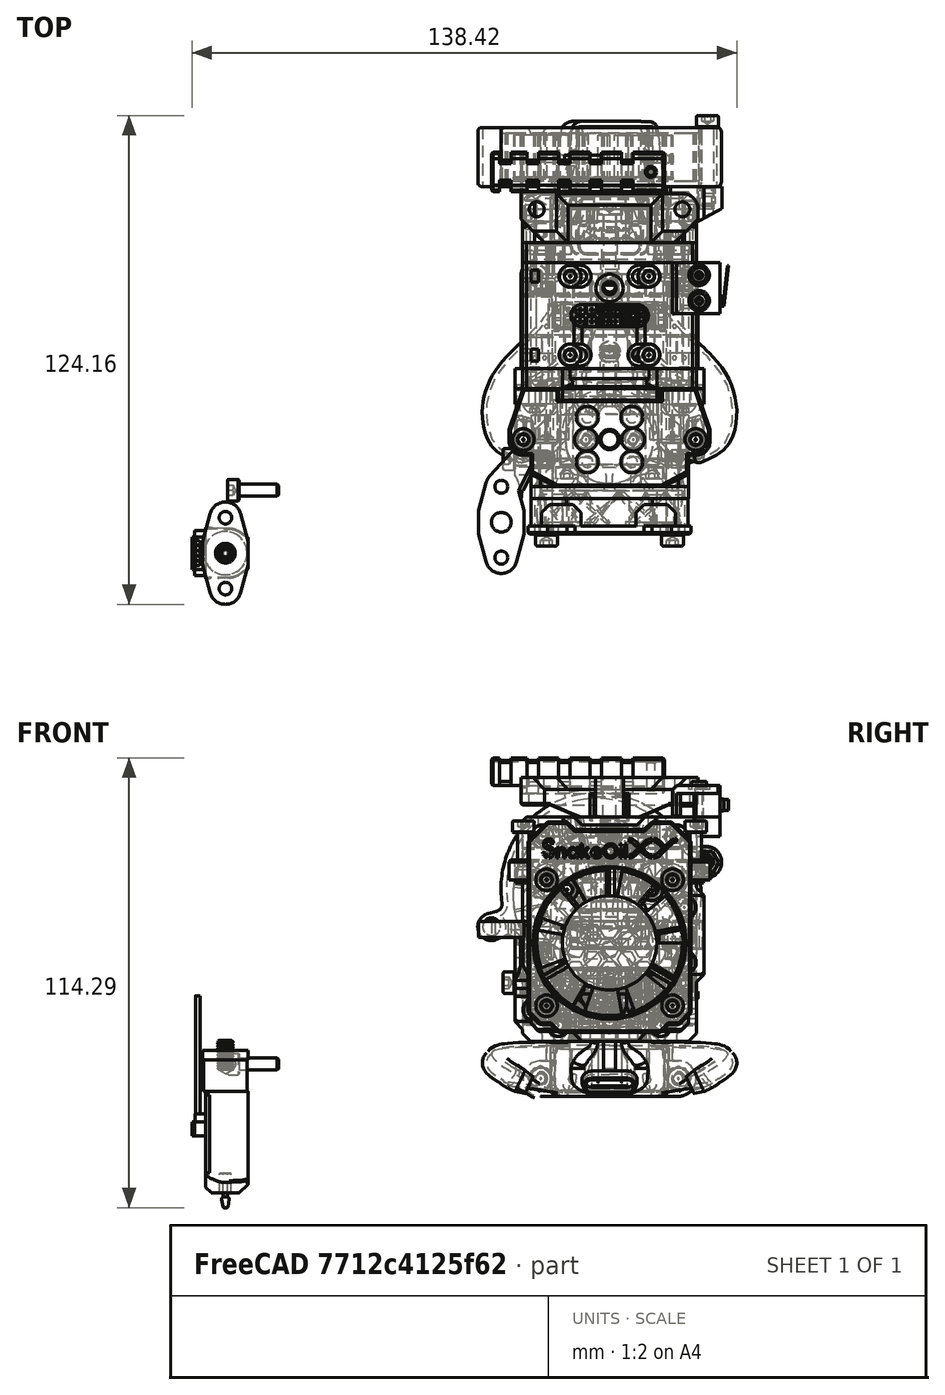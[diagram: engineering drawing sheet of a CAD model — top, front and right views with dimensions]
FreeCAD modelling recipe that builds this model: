
FCSTD DOCUMENT  (FreeCAD 0.19R)
Label: toolhead-sherpa-pcb-1515-assembly
License: Other
LicenseURL: GPL3
objects: Part::FeaturePython×59, Part::Feature×32, App::Part×13, PartDesign::CoordinateSystem×1
note: 92 computed .brp shape members not serialized (recipe doc carries the construction recipe); baked Part::Feature solids carry a one-line shape summary decoded from their .brp

FEATURE [Part::FeaturePython] Screw1373  label="M3x20-Screw024"  # Fasteners workbench fastener (typed FeaturePython)
  Placement = pos=(16,-55.5,30) rot=(1,0,0;1.5708rad)
  baseObject = -> Part__Feature112001131 [Edge124]
  diameter = 4
  invert = false
  leftHanded = false
  length = 10
  lengthCustom = 20
  matchOuter = true
  offset = 2
  thread = false
  type = 33
FEATURE [Part::FeaturePython] Screw1374  label="M3x25-Screw004"  # Fasteners workbench fastener (typed FeaturePython)
  Placement = pos=(-16,-55.5,-2) rot=(1,0,0;1.5708rad)
  baseObject = -> Part__Feature112001131 [Edge127]
  diameter = 4
  invert = false
  leftHanded = false
  length = 10
  lengthCustom = 25
  matchOuter = true
  offset = 2
  thread = false
  type = 33
FEATURE [Part::FeaturePython] Screw1375  label="M3x25-Screw029"  # Fasteners workbench fastener (typed FeaturePython)
  Placement = pos=(16,-55.5,-2) rot=(1,0,0;1.5708rad)
  baseObject = -> Part__Feature112001131 [Edge121]
  diameter = 4
  invert = false
  leftHanded = false
  length = 10
  lengthCustom = 25
  matchOuter = true
  offset = 2
  thread = false
  type = 33
FEATURE [Part::FeaturePython] Screw1376  label="M2.5x12-Screw"  # Fasteners workbench fastener (typed FeaturePython)
  Placement = pos=(-6,-31.5,29.2) rot=(0,0,1;0rad)
  diameter = 3
  invert = false
  leftHanded = false
  length = 10
  lengthCustom = 12
  matchOuter = true
  offset = 10
  thread = false
  type = 33
FEATURE [Part::FeaturePython] Screw1377  label="M2.5x12-Screw001"  # Fasteners workbench fastener (typed FeaturePython)
  Placement = pos=(6,-31.5,29.2) rot=(0,0,1;0rad)
  diameter = 3
  invert = false
  leftHanded = false
  length = 10
  lengthCustom = 12
  matchOuter = true
  offset = 10
  thread = false
  type = 33
FEATURE [Part::FeaturePython] Screw1372  label="M3x20-Screw023"  # Fasteners workbench fastener (typed FeaturePython)
  Placement = pos=(-16,-55.5,30) rot=(1,0,0;1.5708rad)
  baseObject = -> Part__Feature112001131 [Edge130]
  diameter = 4
  invert = false
  leftHanded = false
  length = 10
  lengthCustom = 20
  matchOuter = true
  offset = 2
  thread = false
  type = 33
FEATURE [Part::Feature] Part__Feature112001131  label="4010-fan"
  Placement = pos=(-2.4e-14,-43.5,14) rot=(0,0,1;0rad)
  shape: bbox 40 x 10 x 40 mm, 104 faces (baked)
FEATURE [Part::Feature] Part__Feature112001139  label="BL-touch v3.x002"
  Placement = pos=(-97.5942,-60.3565,-13.2887) rot=(0,0,1;1.5708rad)
  shape: bbox 16.53 x 26.01 x 53.81 mm, 111 faces (baked)
FEATURE [Part::FeaturePython] Nut057  label="M3-Nut026"  # Fasteners workbench fastener (typed FeaturePython)
  Placement = pos=(-17.05,15.5,41) rot=(-1,0,0;1.5708rad)
  diameter = 4
  invert = false
  leftHanded = false
  matchOuter = true
  offset = 0
  thread = false
  type = 7
FEATURE [Part::FeaturePython] Nut004  label="M3-Nut009"  # Fasteners workbench fastener (typed FeaturePython)
  Placement = pos=(13,15.5,-7) rot=(-1,0,0;1.5708rad)
  diameter = 4
  invert = false
  leftHanded = false
  matchOuter = true
  offset = 0
  thread = false
  type = 7
FEATURE [Part::FeaturePython] Nut005  label="M3-Nut030"  # Fasteners workbench fastener (typed FeaturePython)
  Placement = pos=(-13,15.5,-7) rot=(-1,0,0;1.5708rad)
  diameter = 4
  invert = false
  leftHanded = false
  matchOuter = true
  offset = 0
  thread = false
  type = 7
FEATURE [Part::FeaturePython] Screw1359  label="M3x35-Screw004"  # Fasteners workbench fastener (typed FeaturePython)
  Placement = pos=(-13.0042,-16,-6.99647) rot=(1,0,0;1.5708rad)
  diameter = 4
  invert = true
  leftHanded = false
  length = 10
  lengthCustom = 35
  matchOuter = true
  offset = 0
  thread = false
  type = 33
FEATURE [Part::FeaturePython] Screw1360  label="M3x35-Screw003"  # Fasteners workbench fastener (typed FeaturePython)
  Placement = pos=(12.9958,-16,-6.99647) rot=(1,0,0;1.5708rad)
  diameter = 4
  invert = true
  leftHanded = false
  length = 10
  lengthCustom = 35
  matchOuter = true
  offset = 0
  thread = false
  type = 33
FEATURE [Part::FeaturePython] Screw020  label="M3x10-Screw"  # Fasteners workbench fastener (typed FeaturePython)
  Placement = pos=(-10.0042,-9.99647,39.1513) rot=(0,0,1;0rad)
  diameter = 4
  invert = false
  leftHanded = false
  length = 10
  lengthCustom = 10
  matchOuter = true
  offset = 0
  thread = false
  type = 33
FEATURE [Part::FeaturePython] Screw022  label="M3x12-Screw"  # Fasteners workbench fastener (typed FeaturePython)
  Placement = pos=(-21.9,-31.5,42) rot=(0,0,1;0rad)
  diameter = 4
  invert = false
  leftHanded = false
  length = 10
  lengthCustom = 12
  matchOuter = true
  offset = 7
  thread = false
  type = 33
FEATURE [Part::FeaturePython] Screw023  label="M3x12-Screw066"  # Fasteners workbench fastener (typed FeaturePython)
  Placement = pos=(21.9,-31.5,42) rot=(0,0,1;0rad)
  diameter = 4
  invert = false
  leftHanded = false
  length = 10
  lengthCustom = 12
  matchOuter = true
  offset = 7
  thread = false
  type = 33
FEATURE [Part::FeaturePython] Screw026  label="M3x10-Screw199"  # Fasteners workbench fastener (typed FeaturePython)
  Placement = pos=(3e-15,-20.15,-6) rot=(1,0,0;1.5708rad)
  baseObject = -> Part__Feature112001133 [Edge213]
  diameter = 4
  invert = true
  leftHanded = false
  length = 3
  lengthCustom = 10
  matchOuter = true
  offset = 0
  thread = false
  type = 33
FEATURE [Part::FeaturePython] Screw027  label="M3x25-Screw"  # Fasteners workbench fastener (typed FeaturePython)
  Placement = pos=(-10.8,-38.5,27.5) rot=(1,0,0;1.5708rad)
  diameter = 4
  invert = false
  leftHanded = false
  length = 10
  lengthCustom = 25
  matchOuter = true
  offset = 0
  thread = false
  type = 33
FEATURE [Part::FeaturePython] Screw1369  label="M3x25-Screw030"  # Fasteners workbench fastener (typed FeaturePython)
  Placement = pos=(10.8,-38.5,27.5) rot=(1,0,0;1.5708rad)
  diameter = 4
  invert = false
  leftHanded = false
  length = 10
  lengthCustom = 25
  matchOuter = true
  offset = 0
  thread = false
  type = 33
FEATURE [Part::FeaturePython] Nut058  label="M3-Nut027"  # Fasteners workbench fastener (typed FeaturePython)
  Placement = pos=(17.05,15.5,41) rot=(-1,0,0;1.5708rad)
  diameter = 4
  invert = false
  leftHanded = false
  matchOuter = true
  offset = 0
  thread = false
  type = 7
FEATURE [Part::FeaturePython] Screw1355  label="M3x40-Screw001"  # Fasteners workbench fastener (typed FeaturePython)
  Placement = pos=(-18.5,25.5,3.5) rot=(0,-1,0;1.5708rad)
  diameter = 4
  invert = false
  leftHanded = false
  length = 10
  lengthCustom = 40
  matchOuter = true
  offset = 0
  thread = false
  type = 33
FEATURE [Part::FeaturePython] Screw1356  label="M3x40-Screw"  # Fasteners workbench fastener (typed FeaturePython)
  Placement = pos=(18.5,25.5,16.5) rot=(0,1,0;1.5708rad)
  diameter = 4
  invert = false
  leftHanded = false
  length = 10
  lengthCustom = 40
  matchOuter = true
  offset = 0
  thread = false
  type = 33
FEATURE [Part::Feature] Fusion006002011004053036004001028003005014018035002010  label="mosquito-hotend"
  Placement = pos=(0,-31.5,-28) rot=(0,0,1;0rad)
  shape: bbox 27.01 x 18.86 x 47.01 mm, 355 faces, 0 solids (baked)
FEATURE [Part::Feature] Part__Feature112001133  label="mosquito_support"
  Placement = pos=(-2.78e-14,-21.6,27.5) rot=(0,0,1;0rad)
  shape: bbox 40 x 20.25 x 12 mm, 97 faces (baked)
FEATURE [Part::Feature] Part__Feature112001136  label="5015 fan"
  Placement = pos=(-4.23967,32.8,25.9455) rot=(0.15487,0.698575,0.698575;3.44889rad)
  shape: bbox 61.97 x 15 x 62.93 mm, 220 faces (baked)
FEATURE [Part::FeaturePython] Screw1368  label="M3x20-Screw"  # Fasteners workbench fastener (typed FeaturePython)
  Placement = pos=(24.8765,47.8,34.436) rot=(-1,0,0;1.5708rad)
  baseObject = -> Part__Feature112001136 [Edge8]
  diameter = 4
  invert = false
  leftHanded = false
  length = 7
  lengthCustom = 20
  matchOuter = true
  offset = 0
  thread = false
  type = 33
FEATURE [Part::FeaturePython] Screw017  label="M3x10-Screw188"  # Fasteners workbench fastener (typed FeaturePython)
  Placement = pos=(9.99577,10.0035,39.1513) rot=(0,0,1;0rad)
  diameter = 4
  invert = true
  leftHanded = false
  length = 10
  lengthCustom = 10
  matchOuter = true
  offset = 0
  thread = false
  type = 33
FEATURE [Part::FeaturePython] Screw018  label="M3x10-Screw186"  # Fasteners workbench fastener (typed FeaturePython)
  Placement = pos=(9.99577,-9.99647,39.1513) rot=(0,0,1;0rad)
  diameter = 4
  invert = true
  leftHanded = false
  length = 10
  lengthCustom = 10
  matchOuter = true
  offset = 0
  thread = false
  type = 33
FEATURE [Part::FeaturePython] Screw019  label="M3x10-Screw187"  # Fasteners workbench fastener (typed FeaturePython)
  Placement = pos=(-10.0042,10.0035,39.1513) rot=(0,0,1;0rad)
  diameter = 4
  invert = false
  leftHanded = false
  length = 10
  lengthCustom = 10
  matchOuter = true
  offset = 0
  thread = false
  type = 33
FEATURE [Part::FeaturePython] Screw1380  label="M3x35-Screw005"  # Fasteners workbench fastener (typed FeaturePython)
  Placement = pos=(-17.0542,-16.5,41.0035) rot=(1,0,0;1.5708rad)
  diameter = 1
  invert = true
  leftHanded = false
  length = 9
  lengthCustom = 35
  matchOuter = true
  offset = 0
  thread = false
  type = 39
FEATURE [Part::FeaturePython] Screw1381  label="M3x35-Screw"  # Fasteners workbench fastener (typed FeaturePython)
  Placement = pos=(17.0458,-16.5,41.0035) rot=(1,0,0;1.5708rad)
  diameter = 1
  invert = true
  leftHanded = false
  length = 9
  lengthCustom = 35
  matchOuter = true
  offset = 0
  thread = false
  type = 39
FEATURE [Part::Feature] Part__Feature112001143  label="dragon_support"
  Placement = pos=(-1.3e-14,-65.5,-44.5) rot=(1,0,0;3.14159rad)
  shape: bbox 40 x 20.25 x 9.266 mm, 50 faces (baked)
FEATURE [Part::Feature] Chamfer005021077002006007019003014001  label="face-plate"
  Placement = pos=(0,-56.5,-6) rot=(0,0,1;0rad)
  shape: bbox 41.5 x 7.5 x 53.5 mm, 789 faces (baked)
FEATURE [Part::Feature] Chamfer005021077002006007019003032007001  label="mosquito-mount-mod"
  Placement = pos=(0,-31.5,33) rot=(0,0,1;0rad)
  shape: bbox 51.01 x 27.77 x 40.81 mm, 154 faces (baked)
FEATURE [Part::Feature] Chamfer005021077002006007019003029001  label="dragon-mount-mod"
  Placement = pos=(0,-31.5,33) rot=(0,0,1;0rad)
  shape: bbox 51.01 x 26.2 x 43.01 mm, 143 faces (baked)
FEATURE [Part::FeaturePython] Screw1371  label="M3x10-Screw189"  # Fasteners workbench fastener (typed FeaturePython)
  Placement = pos=(-94.0942,-44.3565,-16.7887) rot=(0,-1,0;1.5708rad)
  diameter = 4
  invert = false
  leftHanded = false
  length = 10
  lengthCustom = 10
  matchOuter = true
  offset = 0
  thread = false
  type = 33
FEATURE [App::Part] BL_Touch__1_001  label="BL-Touch <1>001"
  Group = -> [Part__Feature112001139,Screw1371]
  Origin = -> Origin206
  Placement = pos=(70,8,28.5) rot=(0,0,1;0rad)
FEATURE [Part::Feature] Chamfer008009001  label="extruder-belt-tesioner"
  Placement = pos=(6,15,7.5) rot=(0,1,0;3.14159rad)
  shape: bbox 20 x 14.4 x 10 mm, 116 faces (baked)
FEATURE [Part::Feature] Chamfer005021077002006007019003032007003  label="extruder-belt-tesioner001"
  Placement = pos=(-6,15,12.5) rot=(0,0,1;0rad)
  shape: bbox 20 x 14.4 x 10 mm, 116 faces (baked)
FEATURE [Part::Feature] Fusion006002011004053036004001028003005014029  label="endstop-switch"
  Placement = pos=(28,7,46) rot=(0,0,1;1.5708rad)
  shape: bbox 12.18 x 13 x 6 mm, 43 faces (baked)
FEATURE [Part::Feature] Body001001001  label="endstop-cap"
  Placement = pos=(16,7,54) rot=(1,0,0;3.14159rad)
  shape: bbox 12 x 13 x 7.75 mm, 19 faces (baked)
FEATURE [Part::FeaturePython] Screw1382  label="M2x10-Screw001"  # Fasteners workbench fastener (typed FeaturePython)
  Placement = pos=(22.75,3.75,53) rot=(0,0,1;0rad)
  baseObject = -> Body001001001 [Edge27]
  diameter = 2
  invert = false
  leftHanded = false
  length = 5
  lengthCustom = 10
  matchOuter = true
  offset = 0
  thread = false
  type = 33
FEATURE [Part::FeaturePython] Screw1383  label="M2x10-Screw"  # Fasteners workbench fastener (typed FeaturePython)
  Placement = pos=(22.75,10.25,53) rot=(0,0,1;0rad)
  baseObject = -> Body001001001 [Edge25]
  diameter = 2
  invert = false
  leftHanded = false
  length = 5
  lengthCustom = 10
  matchOuter = true
  offset = 0
  thread = false
  type = 33
FEATURE [PartDesign::CoordinateSystem] LCS_toolhead_1515  label="LCS_toolhead-1515"
  AttacherType = Attacher::AttachEngine3D
FEATURE [Part::FeaturePython] HeatSet001  label="M3x4-HeatSet001"  # Fasteners workbench fastener (typed FeaturePython)
  Placement = pos=(-20,-36.5,11.7) rot=(0,-1,0;1.5708rad)
  baseObject = -> Chamfer005021077002006007019003029001 [Edge194]
  diameter = 2
  invert = false
  leftHanded = false
  matchOuter = false
  offset = 0
  thread = false
  type = 25
FEATURE [Part::FeaturePython] HeatSet002  label="M3x4-HeatSet003"  # Fasteners workbench fastener (typed FeaturePython)
  Placement = pos=(20,-36.5,11.7) rot=(0,1,0;1.5708rad)
  baseObject = -> Chamfer005021077002006007019003029001 [Edge128]
  diameter = 2
  invert = true
  leftHanded = false
  matchOuter = false
  offset = 0
  thread = false
  type = 25
FEATURE [Part::FeaturePython] HeatSet003  label="M3x4-HeatSet"  # Fasteners workbench fastener (typed FeaturePython)
  Placement = pos=(20,-36.5,3.7) rot=(0,1,0;1.5708rad)
  baseObject = -> Chamfer005021077002006007019003029001 [Edge127]
  diameter = 2
  invert = true
  leftHanded = false
  matchOuter = false
  offset = 0
  thread = false
  type = 25
FEATURE [Part::FeaturePython] HeatSet004  label="M3x4-HeatSet009"  # Fasteners workbench fastener (typed FeaturePython)
  Placement = pos=(1e-14,7.5,46) rot=(0,0,1;0rad)
  diameter = 2
  invert = true
  leftHanded = false
  matchOuter = false
  offset = 0
  thread = false
  type = 25
FEATURE [Part::FeaturePython] HeatSet014  label="M3x4-HeatSet010"  # Fasteners workbench fastener (typed FeaturePython)
  Placement = pos=(10.8,-13.5,27.705) rot=(-1,0,0;1.5708rad)
  diameter = 2
  invert = true
  leftHanded = false
  matchOuter = false
  offset = 0
  thread = false
  type = 25
FEATURE [Part::FeaturePython] HeatSet015  label="M3x4-HeatSet012"  # Fasteners workbench fastener (typed FeaturePython)
  Placement = pos=(-10.8,-13.5,27.71) rot=(-1,0,0;1.5708rad)
  diameter = 2
  invert = true
  leftHanded = false
  matchOuter = false
  offset = 0
  thread = false
  type = 25
FEATURE [Part::FeaturePython] HeatSet016  label="M3x4-HeatSet004"  # Fasteners workbench fastener (typed FeaturePython)
  Placement = pos=(10,25.5,3.5) rot=(0,1,0;1.5708rad)
  baseObject = -> Chamfer008009001 [Edge5]
  diameter = 2
  invert = false
  leftHanded = false
  matchOuter = false
  offset = 0
  thread = false
  type = 25
FEATURE [Part::FeaturePython] HeatSet017  label="M3x4-HeatSet013"  # Fasteners workbench fastener (typed FeaturePython)
  Placement = pos=(-10,25.5,16.5) rot=(0,-1,0;1.5708rad)
  baseObject = -> Chamfer005021077002006007019003032007003 [Edge5]
  diameter = 2
  invert = false
  leftHanded = false
  matchOuter = false
  offset = 0
  thread = false
  type = 25
FEATURE [Part::FeaturePython] HeatSet018  label="M3x4-HeatSet018"  # Fasteners workbench fastener (typed FeaturePython)
  Placement = pos=(21.9,-31.5,35) rot=(0,0,1;0rad)
  baseObject = -> Chamfer005021077002006007019003029001 [Edge25]
  diameter = 2
  invert = false
  leftHanded = false
  matchOuter = false
  offset = 0
  thread = false
  type = 25
FEATURE [Part::FeaturePython] HeatSet019  label="M3x4-HeatSet017"  # Fasteners workbench fastener (typed FeaturePython)
  Placement = pos=(-21.9,-31.5,35) rot=(0,0,1;0rad)
  baseObject = -> Chamfer005021077002006007019003029001 [Edge1]
  diameter = 2
  invert = false
  leftHanded = false
  matchOuter = false
  offset = 0
  thread = false
  type = 25
FEATURE [Part::Feature] Part__Feature003  label="duct-tri-horn"
  Placement = pos=(0,10.5978,-18) rot=(1,0,0;1.5708rad)
  shape: bbox 65.34 x 50.74 x 15.61 mm, 106 faces (baked)
FEATURE [Part::FeaturePython] Nut059  label="M3-Nut032"  # Fasteners workbench fastener (typed FeaturePython)
  Placement = pos=(-17.5,8.59783,-20.5) rot=(1,0,0;1.5708rad)
  baseObject = -> Part__Feature003 [Edge75]
  diameter = 4
  invert = false
  leftHanded = false
  matchOuter = true
  offset = 0
  thread = false
  type = 7
FEATURE [Part::FeaturePython] Nut060  label="M3-Nut033"  # Fasteners workbench fastener (typed FeaturePython)
  Placement = pos=(17.5,8.59783,-20.5) rot=(1,0,0;1.5708rad)
  baseObject = -> Part__Feature003 [Edge202]
  diameter = 4
  invert = true
  leftHanded = false
  matchOuter = true
  offset = 0
  thread = false
  type = 7
FEATURE [Part::FeaturePython] Screw1384  label="M3x12-Screw075"  # Fasteners workbench fastener (typed FeaturePython)
  Placement = pos=(17.5,18.5,-20.5) rot=(-1,0,0;1.5708rad)
  diameter = 4
  invert = false
  leftHanded = false
  length = 4
  lengthCustom = 12
  matchOuter = true
  offset = 0
  thread = false
  type = 34
FEATURE [Part::FeaturePython] Screw1385  label="M3x12-Screw074"  # Fasteners workbench fastener (typed FeaturePython)
  Placement = pos=(-17.5,18.5,-20.5) rot=(-1,0,0;1.5708rad)
  diameter = 4
  invert = true
  leftHanded = false
  length = 4
  lengthCustom = 12
  matchOuter = true
  offset = 0
  thread = false
  type = 34
FEATURE [Part::FeaturePython] HeatSet024  label="M3-HeatSet"  # Fasteners workbench fastener (typed FeaturePython)
  Placement = pos=(1.1e-14,13.5,42) rot=(-1,0,0;1.5708rad)
  diameter = 2
  invert = false
  leftHanded = false
  matchOuter = false
  offset = 0
  thread = false
  type = 25
FEATURE [Part::FeaturePython] HeatSet  label="M3x4-HeatSet019"  # Fasteners workbench fastener (typed FeaturePython)
  Placement = pos=(24.5,32.75,34.5) rot=(-1,0,0;1.5708rad)
  diameter = 2
  invert = false
  leftHanded = false
  matchOuter = false
  offset = 0
  thread = false
  type = 25
FEATURE [Part::Feature] Part__Feature  label="bltouch-mount"
  Placement = pos=(0.5,-31.5,15.4) rot=(0,0,1;0rad)
  shape: bbox 13.25 x 33 x 19 mm, 31 faces (baked)
FEATURE [Part::FeaturePython] Screw1387  label="M3x10-Screw190"  # Fasteners workbench fastener (typed FeaturePython)
  Placement = pos=(-24,-36.5,3.9) rot=(0,-1,0;1.5708rad)
  baseObject = -> Part__Feature [Edge2]
  diameter = 4
  invert = false
  leftHanded = false
  length = 3
  lengthCustom = 10
  matchOuter = true
  offset = 0
  thread = false
  type = 34
FEATURE [Part::Feature] Chamfer008011001001001001  label="extruder-belt-clamp-r004"
  Placement = pos=(0,-13,7.5) rot=(1,0,0;1.5708rad)
  shape: bbox 10.5 x 4.5 x 20 mm, 69 faces (baked)
FEATURE [Part::Feature] Chamfer005021077002006007019003032018001002  label="extruder-belt-clamp-r005"
  Placement = pos=(2e-15,-13,12.5) rot=(0,0.707107,-0.707107;3.14159rad)
  shape: bbox 10.5 x 4.5 x 20 mm, 69 faces (baked)
FEATURE [Part::FeaturePython] Washer  label="M3-Washer"  # Fasteners workbench fastener (typed FeaturePython)
  Placement = pos=(-19,-22.5,11) rot=(1,0,0;1.5708rad)
  baseObject = -> Chamfer005021077002006007019003032018001002 [Edge85]
  diameter = 4
  invert = false
  leftHanded = false
  matchOuter = true
  offset = 0
  type = 5
FEATURE [Part::FeaturePython] Washer001  label="M3-Washer006"  # Fasteners workbench fastener (typed FeaturePython)
  Placement = pos=(-19,-22.5,-3) rot=(1,0,0;1.5708rad)
  baseObject = -> Chamfer005021077002006007019003032018001002 [Edge84]
  diameter = 4
  invert = false
  leftHanded = false
  matchOuter = true
  offset = 0
  type = 5
FEATURE [Part::FeaturePython] Washer002  label="M3-Washer004"  # Fasteners workbench fastener (typed FeaturePython)
  Placement = pos=(19,-22.5,23) rot=(1,0,0;1.5708rad)
  baseObject = -> Chamfer008011001001001001 [Edge84]
  diameter = 4
  invert = false
  leftHanded = false
  matchOuter = true
  offset = 0
  type = 5
FEATURE [Part::FeaturePython] Washer003  label="M3-Washer005"  # Fasteners workbench fastener (typed FeaturePython)
  Placement = pos=(19,-22.5,9) rot=(1,0,0;1.5708rad)
  baseObject = -> Chamfer008011001001001001 [Edge85]
  diameter = 4
  invert = false
  leftHanded = false
  matchOuter = true
  offset = 0
  type = 5
FEATURE [Part::FeaturePython] Screw1388  label="M3x10-Screw195"  # Fasteners workbench fastener (typed FeaturePython)
  Placement = pos=(19,-23.05,23) rot=(1,0,0;1.5708rad)
  baseObject = -> Washer002 [Edge1]
  diameter = 1
  invert = false
  leftHanded = false
  length = 2
  lengthCustom = 10
  matchOuter = true
  offset = 0
  thread = false
  type = 40
FEATURE [Part::FeaturePython] Screw1389  label="M3x10-Screw196"  # Fasteners workbench fastener (typed FeaturePython)
  Placement = pos=(19,-23.05,9) rot=(1,0,0;1.5708rad)
  baseObject = -> Washer003 [Edge1]
  diameter = 1
  invert = false
  leftHanded = false
  length = 2
  lengthCustom = 10
  matchOuter = true
  offset = 0
  thread = false
  type = 40
FEATURE [Part::FeaturePython] Screw1390  label="M3x10-Screw198"  # Fasteners workbench fastener (typed FeaturePython)
  Placement = pos=(-19,-23.05,11) rot=(1,0,0;1.5708rad)
  baseObject = -> Washer [Edge1]
  diameter = 1
  invert = false
  leftHanded = false
  length = 2
  lengthCustom = 10
  matchOuter = true
  offset = 0
  thread = false
  type = 40
FEATURE [Part::FeaturePython] Screw1391  label="M3x10-Screw197"  # Fasteners workbench fastener (typed FeaturePython)
  Placement = pos=(-19,-23.05,-3) rot=(1,0,0;1.5708rad)
  baseObject = -> Washer001 [Edge1]
  diameter = 1
  invert = false
  leftHanded = false
  length = 2
  lengthCustom = 10
  matchOuter = true
  offset = 0
  thread = false
  type = 40
FEATURE [Part::Feature] Part__Feature112001168  label="SOLID004"
  shape: bbox 12.4 x 5.75 x 10.4 mm, 141 faces (baked)
FEATURE [App::Part] JST_XH_B04B_XH_A_1x04_P2_50mm_Vertical  label="JST_XH_B04B-XH-A_1x04_P2.50mm_Vertical"
  Group = -> [Part__Feature112001168]
  Origin = -> Origin216
  Placement = pos=(-8.5,-2.75,1.65) rot=(0,0,1;3.14159rad)
FEATURE [Part::Feature] Part__Feature112001167  label="SOLID003"
  shape: bbox 9.9 x 5.75 x 10.4 mm, 117 faces (baked)
FEATURE [Part::FeaturePython] Screw  label="M3x12-Screw076"  # Fasteners workbench fastener (typed FeaturePython)
  Placement = pos=(0,25.5,42) rot=(-1,0,0;1.5708rad)
  diameter = 4
  invert = true
  leftHanded = false
  length = 4
  lengthCustom = 12
  matchOuter = true
  offset = 0
  thread = false
  type = 34
FEATURE [Part::Feature] Part__Feature112001170  label="SOLID006"
  shape: bbox 2 x 1.25 x 1.25 mm, 28 faces (baked)
FEATURE [App::Part] C_0805_2012Metric
  Group = -> [Part__Feature112001170]
  Origin = -> Origin218
  Placement = pos=(-20.5,-3.225,1.65) rot=(0,0,1;1.5708rad)
FEATURE [Part::Feature] Part__Feature112001169  label="SOLID005"
  shape: bbox 14.9 x 5.75 x 10.4 mm, 165 faces (baked)
FEATURE [App::Part] JST_XH_B05B_XH_A_1x05_P2_50mm_Vertical  label="JST_XH_B05B-XH-A_1x05_P2.50mm_Vertical"
  Group = -> [Part__Feature112001169]
  Origin = -> Origin217
  Placement = pos=(-9,-10.75,1.65) rot=(0,0,1;3.14159rad)
FEATURE [App::Part] JST_XH_B03B_XH_A_1x03_P2_50mm_Vertical001  label="JST_XH_B03B-XH-A_1x03_P2.50mm_Vertical001"
  Group = -> [Part__Feature112001167]
  Origin = -> Origin215
  Placement = pos=(4,-2.75,1.65) rot=(0,0,1;3.14159rad)
FEATURE [Part::Feature] Part__Feature112001166  label="SOLID002"
  shape: bbox 7.4 x 5.75 x 10.4 mm, 89 faces (baked)
FEATURE [App::Part] JST_XH_B02B_XH_A_1x02_P2_50mm_Vertical001  label="JST_XH_B02B-XH-A_1x02_P2.50mm_Vertical001"
  Group = -> [Part__Feature112001166]
  Origin = -> Origin214
  Placement = pos=(9.5,-10.75,1.65) rot=(0,0,1;3.14159rad)
FEATURE [Part::Feature] Part__Feature112001171  label="COMPOUND002"
  shape: bbox 45 x 28.5 x 1.6 mm, 50 faces (baked)
FEATURE [Part::Feature] Part__Feature112001163  label="SOLID"
  shape: bbox 9.9 x 5.75 x 10.4 mm, 117 faces (baked)
FEATURE [Part::Feature] Part__Feature112001165  label="SOLID001"
  shape: bbox 7.4 x 5.75 x 10.4 mm, 89 faces (baked)
FEATURE [App::Part] JST_XH_B02B_XH_A_1x02_P2_50mm_Vertical  label="JST_XH_B02B-XH-A_1x02_P2.50mm_Vertical"
  Group = -> [Part__Feature112001165]
  Origin = -> Origin213
  Placement = pos=(19,-10.75,1.65) rot=(0,0,1;3.14159rad)
FEATURE [Part::Feature] Part__Feature112001164  label="COMPOUND"
  shape: bbox 28.15 x 8.8 x 13.09 mm, 388 faces (baked)
FEATURE [App::Part] COMPOUND  label="COMPOUND001"
  Group = -> [Part__Feature112001164]
  Origin = -> Origin211
FEATURE [App::Part] microfit_16  label="microfit-16"
  Group = -> [COMPOUND]
  Origin = -> Origin212
  Placement = pos=(-6e-06,6.81,6.65) rot=(0,0,1;0rad)
FEATURE [App::Part] JST_XH_B03B_XH_A_1x03_P2_50mm_Vertical  label="JST_XH_B03B-XH-A_1x03_P2.50mm_Vertical"
  Group = -> [Part__Feature112001163]
  Origin = -> Origin210
  Placement = pos=(16.5,-2.75,1.65) rot=(0,0,1;3.14159rad)
FEATURE [Part::FeaturePython] Screw001  label="M3x6-Screw001"  # Fasteners workbench fastener (typed FeaturePython)
  Placement = pos=(18.5,10.25,1.6) rot=(0,0,1;0rad)
  baseObject = -> Part__Feature112001171 [Edge78]
  diameter = 4
  invert = false
  leftHanded = false
  length = 1
  lengthCustom = 6
  matchOuter = true
  offset = 0
  thread = false
  type = 34
FEATURE [Part::FeaturePython] Screw002  label="M3x6-Screw"  # Fasteners workbench fastener (typed FeaturePython)
  Placement = pos=(-18.5,10.25,1.6) rot=(0,0,1;0rad)
  baseObject = -> Part__Feature112001171 [Edge81]
  diameter = 4
  invert = false
  leftHanded = false
  length = 1
  lengthCustom = 6
  matchOuter = true
  offset = 0
  thread = false
  type = 34
FEATURE [Part::FeaturePython] Screw003  label="M3x20-Screw025"  # Fasteners workbench fastener (typed FeaturePython)
  Placement = pos=(0,-9.25,1.6) rot=(0,0,1;0rad)
  baseObject = -> Part__Feature112001171 [Edge92]
  diameter = 4
  invert = false
  leftHanded = false
  length = 7
  lengthCustom = 20
  matchOuter = true
  offset = 0
  thread = false
  type = 34
FEATURE [App::Part] Open_CASCADE_STEP_translator_6_9_1  label="PCB-rev1"
  Group = -> [JST_XH_B03B_XH_A_1x03_P2_50mm_Vertical,microfit_16,JST_XH_B02B_XH_A_1x02_P2_50mm_Vertical,JST_XH_B02B_XH_A_1x02_P2_50mm_Vertical001,JST_XH_B03B_XH_A_1x03_P2_50mm_Vertical001,JST_XH_B04B_XH_A_1x04_P2_50mm_Vertical,JST_XH_B05B_XH_A_1x05_P2_50mm_Vertical,C_0805_2012Metric,Part__Feature112001171,Screw002,Screw001,Screw003]
  Origin = -> Origin219
  Placement = pos=(0,16.8,56) rot=(0,0,1;0rad)
FEATURE [Part::Feature] Chamfer001002006005073001  label="pcb-mounter-cable-guide"
  Placement = pos=(0,29.5,32) rot=(1,0,0;1.5708rad)
  shape: bbox 52.5 x 23 x 29 mm, 192 faces (baked)
FEATURE [Part::Feature] Tube001  label="pcb_spacer"
  Placement = pos=(0,7,46) rot=(0,0,1;0rad)
  shape: bbox 7 x 7 x 10 mm, 4 faces (baked)
FEATURE [App::Part] Part  label="toolhead-pcb"
  Group = -> [Open_CASCADE_STEP_translator_6_9_1,Screw,Chamfer001002006005073001,Tube001]
  Origin = -> Origin
FEATURE [Part::Feature] Chamfer008009  label="extruder-front-plate"
  Placement = pos=(0,-13,10) rot=(1,0,0;1.5708rad)
  shape: bbox 48 x 8 x 57 mm, 192 faces (baked)
FEATURE [Part::Feature] Chamfer001  label="extruderbottom-plate"
  Placement = pos=(0,17.6,-29.8) rot=(1,0,0;1.5708rad)
  shape: bbox 44.1 x 27 x 22.2 mm, 100 faces (baked)
FEATURE [Part::FeaturePython] HeatSet025  label="M3x4-HeatSet020"  # Fasteners workbench fastener (typed FeaturePython)
  Placement = pos=(0,-13.5,-5.8) rot=(1,0,0;1.5708rad)
  baseObject = -> Chamfer001 [Edge50]
  diameter = 3
  invert = false
  leftHanded = false
  matchOuter = false
  offset = 0
  thread = false
  type = 25
FEATURE [Part::Feature] Chamfer005021077002006007019003032020001  label="extruder-back-plate"
  Placement = pos=(1e-15,10,10) rot=(0,0.707107,0.707107;3.14159rad)
  shape: bbox 51.76 x 37.05 x 72.2 mm, 534 faces (baked)
FEATURE [Part::Feature] Body001002004  label="top-plate-with-endstop"
  Placement = pos=(0,0,0) rot=(0,0,1;3.14159rad)
  shape: bbox 50.05 x 27 x 15.5 mm, 97 faces (baked)
FEATURE [App::Part] Part197  label="toolhead-sherp-pcb-1515"
  Group = -> [Fusion006002011004053036004001028003005014018035002010,Part__Feature112001133,Part__Feature112001136,Part__Feature112001131,BL_Touch__1_001,Nut058,Nut005,Nut004,Screw1355,Screw1356,Nut057,Screw1360,Screw1359,Screw1368,Screw022,Screw018,Screw020,Screw023,Screw019,Screw017,Screw026,Screw1376,Screw1377,Screw1369,Screw027,Screw1373,Screw1375,Screw1374,Screw1372,Screw1381,Screw1380,+46 more]
  Origin = -> Origin205
  Placement = pos=(0,31.5,-33) rot=(0,0,1;0rad)
